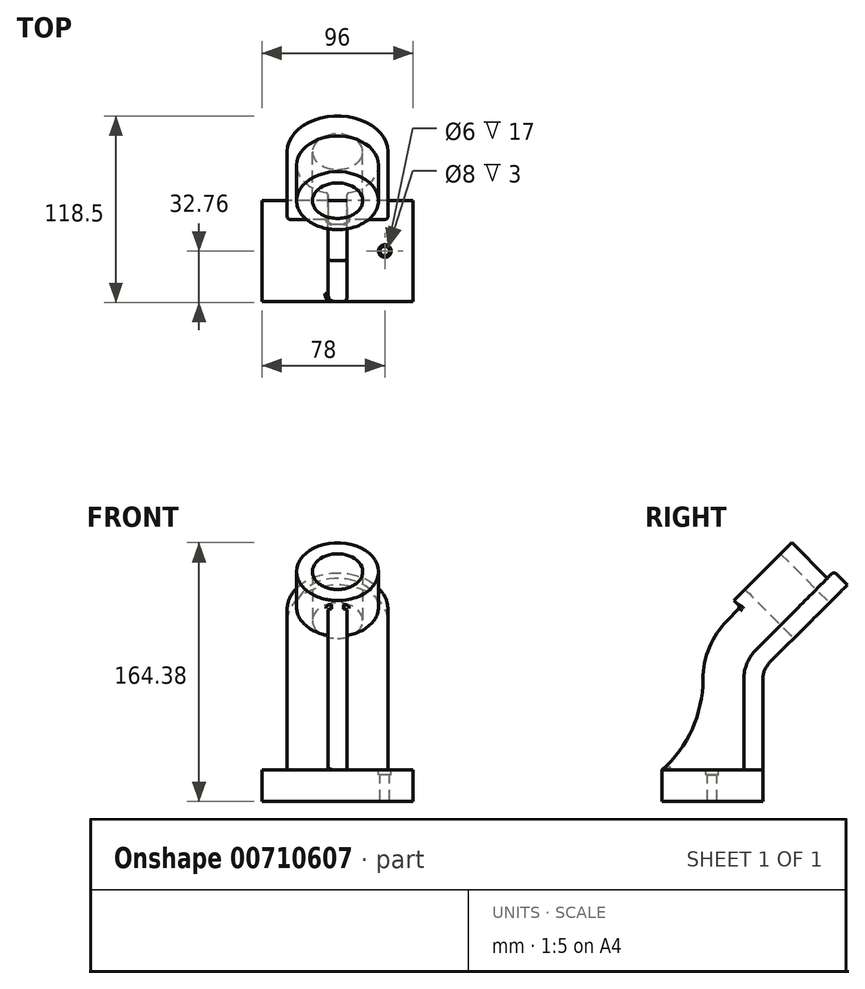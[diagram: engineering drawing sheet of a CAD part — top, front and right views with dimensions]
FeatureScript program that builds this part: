
annotation { "Feature Type Name" : "Feature", "Feature Type Description" : "" }
export const myFeature = defineFeature(function(context is Context, id is Id, definition is map)
    precondition{}
    {
        {
            var Q0;
            Q0=qCreatedBy(makeId("Top.planeOp"),FACE);
            var sketch = newSketch(context, id + "F0", { "sketchPlane" : qUnion([Q0])});
            skLineSegment(sketch, "E0.bottom", {"start": v(-48, 0) * mm, "end": v(48, 0) * mm});
            skLineSegment(sketch, "E0.top", {"start": v(-48, -64) * mm, "end": v(48, -64) * mm});
            skLineSegment(sketch, "E0.left", {"start": v(-48, 0) * mm, "end": v(-48, -64) * mm});
            skLineSegment(sketch, "E0.right", {"start": v(48, 0) * mm, "end": v(48, -64) * mm});
            skPoint(sketch, "E1", {"position": v(0, 0) * mm});
            skSolve(sketch);
        }
        {
            var Q0;
            Q0 = qSketchRegion(id + "F0", true);
            extrude(context, id + "F1", {"entities" : qUnion([Q0]), "depth" : 20 * mm, "offsetDistance" : 25 * mm});
        }
        {
            var Q0;
            Q0=qCreatedBy(makeId("Right.planeOp"),FACE);
            var sketch = newSketch(context, id + "F2", { "sketchPlane" : qUnion([Q0])});
            skLineSegment(sketch, "E2", {"start": v(0, 20) * mm, "end": v(0, 77.56) * mm});
            skLineSegment(sketch, "E3", {"start": v(4.4, 88.17) * mm, "end": v(53.74, 137.51) * mm});
            skLineSegment(sketch, "E4", {"start": v(31.11, 114.89) * mm, "end": v(0, 146) * mm, "construction": true});
            skPoint(sketch, "E5.visualSharp", {"position": v(0, 83.77) * mm});
            skArc(sketch, "E5.filletArc", {"start": v(4.4, 88.17) * mm, "mid": v(1.14, 83.3) * mm, "end": v(0, 77.56) * mm});
            skLineSegment(sketch, "E6.0", {"start": v(-4.1, 96.65) * mm, "end": v(45.25, 146) * mm});
            skArc(sketch, "E6.1", {"start": v(-4.1, 96.65) * mm, "mid": v(-9.94, 87.9) * mm, "end": v(-12, 77.56) * mm});
            skLineSegment(sketch, "E6.2", {"start": v(-12, 20) * mm, "end": v(-12, 77.56) * mm});
            skLineSegment(sketch, "E7", {"start": v(45.25, 146) * mm, "end": v(53.74, 137.51) * mm});
            skLineSegment(sketch, "E8", {"start": v(0, 20) * mm, "end": v(-12, 20) * mm});
            skPoint(sketch, "E9", {"position": v(22.63, 123.37) * mm});
            skSolve(sketch);
        }
        {
            var Q0;
            Q0 = qSketchRegion(id + "F2", true);
            extrude(context, id + "F3", {"entities" : qUnion([Q0]), "operationType" : NewBodyOperationType.ADD, "endBound" : BoundingType.SYMMETRIC, "depth" : 64 * mm, "offsetDistance" : 25 * mm});
        }
        {
            var Q0;
            Q0=makeQuery(id+"F3.opExtrude","CAP_EDGE",EDGE,{"disambiguationData":[OSD([sQuery(id+"F2.wireOp",EDGE,"E7")])],"isStart":false});
            var Q1;
            Q1=makeQuery(id+"F3.opExtrude","CAP_EDGE",EDGE,{"disambiguationData":[OSD([sQuery(id+"F2.wireOp",EDGE,"E7")])],"isStart":true});
            fillet(context, id + "F4", {"entities" : qUnion([Q0, Q1]), "radius" : 32 * mm, "tangentPropagation" : true, "allowEdgeOverflow" : false});
        }
        {
            var Q0;
            Q0=makeQuery(id+"F3.opExtrude","SWEPT_FACE",FACE,{"disambiguationData":[OSD([sQuery(id+"F2.wireOp",EDGE,"E6.0")])]});
            var sketch = newSketch(context, id + "F5", { "sketchPlane" : qUnion([Q0])});
            skCircle(sketch, "E10", {"center": v(0, 103.24) * mm, "radius": 16 * mm});
            skCircle(sketch, "E11", {"center": v(0, 103.24) * mm, "radius": 26 * mm});
            skSolve(sketch);
        }
        {
            var Q0;
            Q0 = qSketchRegion(id + "F5", true);
            var Q1;
            Q1=sQuery(id+"F2.wireOp",VERTEX,"E4.end");
            extrude(context, id + "F6", {"entities" : qUnion([Q0]), "operationType" : NewBodyOperationType.ADD, "endBound" : BoundingType.UP_TO_VERTEX, "depth" : 32 * mm, "endBoundEntityVertex" : qUnion([Q1]), "offsetDistance" : 25 * mm});
        }
        {
            var Q0;
            Q0=makeQuery(id+"F5.imprint","IMPRINT",FACE,{"disambiguationData":[TD([[makeQuery(id+"F5.imprint","IMPRINT",EDGE,{"derivedFrom":sQuery(id+"F5.wireOp",EDGE,"E10")}),1.0]])]});
            extrude(context, id + "F7", {"entities" : qUnion([Q0]), "operationType" : NewBodyOperationType.REMOVE, "endBound" : BoundingType.THROUGH_ALL, "oppositeDirection" : true, "depth" : 25 * mm, "offsetDistance" : 25 * mm});
        }
        {
            var Q0;
            Q0=qCreatedBy(makeId("Right.planeOp"),FACE);
            var sketch = newSketch(context, id + "F8", { "sketchPlane" : qUnion([Q0])});
            skLineSegment(sketch, "E12.0", {"start": v(-11.31, 134.69) * mm, "end": v(11.31, 157.31) * mm, "construction": true});
            skLineSegment(sketch, "E13.0", {"start": v(-4.1, 96.65) * mm, "end": v(11.31, 112.06) * mm});
            skArc(sketch, "E14.0", {"start": v(-4.1, 96.65) * mm, "mid": v(-9.94, 87.9) * mm, "end": v(-12, 77.56) * mm});
            skLineSegment(sketch, "E15.0", {"start": v(-12, 20) * mm, "end": v(-12, 77.56) * mm});
            skLineSegment(sketch, "E16", {"start": v(-7.07, 130.44) * mm, "end": v(11.31, 112.06) * mm});
            skPoint(sketch, "E17.orphan", {"position": v(22.63, 123.37) * mm});
            skLineSegment(sketch, "E18.0", {"start": v(-22.48, 115.04) * mm, "end": v(-7.07, 130.44) * mm});
            skArc(sketch, "E18.1", {"start": v(-22.48, 115.04) * mm, "mid": v(-33.97, 97.84) * mm, "end": v(-38, 77.56) * mm});
            skArc(sketch, "E19", {"start": v(-64, 20) * mm, "mid": v(-44.8, 45.98) * mm, "end": v(-38, 77.56) * mm});
            skLineSegment(sketch, "E20", {"start": v(-64, 20) * mm, "end": v(-12, 20) * mm});
            skLineSegment(sketch, "E21", {"start": v(-38, 77.56) * mm, "end": v(-38, 77.56) * mm});
            skSolve(sketch);
        }
        {
            var Q0;
            Q0 = qSketchRegion(id + "F8", true);
            extrude(context, id + "F9", {"entities" : qUnion([Q0]), "operationType" : NewBodyOperationType.ADD, "endBound" : BoundingType.SYMMETRIC, "depth" : 12 * mm, "offsetDistance" : 25 * mm});
        }
        {
            var Q0;
            Q0 = qSketchRegion(id + "F8", true);
            extrude(context, id + "F10", {"entities" : qUnion([Q0]), "operationType" : NewBodyOperationType.ADD, "endBound" : BoundingType.SYMMETRIC, "depth" : 12 * mm, "offsetDistance" : 25 * mm});
        }
        {
            var Q0;
            {var subQ1=sQuery(id+"F0.wireOp",EDGE,"E0.top");var subQ3=sQuery(id+"F0.wireOp",EDGE,"E0.right");var subQ4=sQuery(id+"F0.wireOp",EDGE,"E0.bottom");Q0=makeQuery(id+"F9.boolean.opBoolean","SPLIT",FACE,{"disambiguationData":[TD([makeQuery(id+"F1.opExtrude","SWEPT_FACE",FACE,{"disambiguationData":[OSD([subQ3])]})])],"derivedFrom":makeQuery(id+"F1.opExtrude","CAP_FACE",FACE,{"disambiguationData":[OSD([subQ4,subQ1,sQuery(id+"F0.wireOp",EDGE,"E0.left"),subQ3])],"isStart":false})});}
            var sketch = newSketch(context, id + "F11", { "sketchPlane" : qUnion([Q0])});
            skCircle(sketch, "E22", {"center": v(30, -32) * mm, "radius": 3 * mm});
            skCircle(sketch, "E23", {"center": v(30, -32) * mm, "radius": 4 * mm});
            skLineSegment(sketch, "E24", {"start": v(0, 0) * mm, "end": v(0, -64) * mm, "construction": true});
            skSolve(sketch);
        }
        {
            var Q0;
            Q0=makeQuery(id+"F11.imprint","IMPRINT",FACE,{"disambiguationData":[TD([[makeQuery(id+"F11.imprint","IMPRINT",EDGE,{"derivedFrom":sQuery(id+"F11.wireOp",EDGE,"E22")}),1.0]])]});
            extrude(context, id + "F12", {"entities" : qUnion([Q0]), "operationType" : NewBodyOperationType.REMOVE, "endBound" : BoundingType.THROUGH_ALL, "oppositeDirection" : true, "depth" : 25 * mm, "offsetDistance" : 25 * mm});
        }
        {
            var Q0;
            Q0=makeQuery(id+"F11.imprint","IMPRINT",FACE,{"disambiguationData":[TD([[makeQuery(id+"F11.imprint","IMPRINT",EDGE,{"derivedFrom":sQuery(id+"F11.wireOp",EDGE,"E22")}),-1.0]])]});
            extrude(context, id + "F13", {"entities" : qUnion([Q0]), "operationType" : NewBodyOperationType.REMOVE, "oppositeDirection" : true, "depth" : 3 * mm, "offsetDistance" : 25 * mm});
        }
        {
            var Q0;
            Q0=makeQuery(id+"F6.opExtrude","CAP_EDGE",EDGE,{"disambiguationData":[OSD([sQuery(id+"F5.wireOp",EDGE,"E11")])],"isStart":true});
            var Q1;
            Q1=makeQuery(id+"F9.opExtrude","CAP_EDGE",EDGE,{"disambiguationData":[OSD([sQuery(id+"F8.wireOp",EDGE,"E13.0")])],"isStart":true});
            var Q2;
            Q2=makeQuery(id+"F9.opExtrude","CAP_EDGE",EDGE,{"disambiguationData":[OSD([sQuery(id+"F8.wireOp",EDGE,"E13.0")])],"isStart":false});
            var Q3;
            Q3=makeQuery(id+"F9.boolean.opBoolean","INTERSECT",EDGE,{"derivedFrom":[makeQuery(id+"F6.opExtrude","SWEPT_FACE",FACE,{"disambiguationData":[OSD([sQuery(id+"F5.wireOp",EDGE,"E11")])]}),makeQuery(id+"F9.opExtrude","SWEPT_FACE",FACE,{"disambiguationData":[OSD([sQuery(id+"F8.wireOp",EDGE,"E18.0")])]})]});
            var Q4;
            Q4=makeQuery(id+"F9.boolean.opBoolean","INTERSECT",EDGE,{"derivedFrom":[makeQuery(id+"F6.opExtrude","SWEPT_FACE",FACE,{"disambiguationData":[OSD([sQuery(id+"F5.wireOp",EDGE,"E11")])]}),makeQuery(id+"F9.opExtrude","CAP_FACE",FACE,{"disambiguationData":[OSD([sQuery(id+"F8.wireOp",EDGE,"E13.0"),sQuery(id+"F8.wireOp",EDGE,"E14.0"),sQuery(id+"F8.wireOp",EDGE,"E15.0"),sQuery(id+"F8.wireOp",EDGE,"E16"),sQuery(id+"F8.wireOp",EDGE,"E18.0"),sQuery(id+"F8.wireOp",EDGE,"E18.1"),sQuery(id+"F8.wireOp",EDGE,"E19"),sQuery(id+"F8.wireOp",EDGE,"E20"),sQuery(id+"F8.wireOp",EDGE,"E21")])],"isStart":true})]});
            var Q5;
            Q5=makeQuery(id+"F9.boolean.opBoolean","INTERSECT",EDGE,{"derivedFrom":[makeQuery(id+"F6.opExtrude","SWEPT_FACE",FACE,{"disambiguationData":[OSD([sQuery(id+"F5.wireOp",EDGE,"E11")])]}),makeQuery(id+"F9.opExtrude","CAP_FACE",FACE,{"disambiguationData":[OSD([sQuery(id+"F8.wireOp",EDGE,"E13.0"),sQuery(id+"F8.wireOp",EDGE,"E14.0"),sQuery(id+"F8.wireOp",EDGE,"E15.0"),sQuery(id+"F8.wireOp",EDGE,"E16"),sQuery(id+"F8.wireOp",EDGE,"E18.0"),sQuery(id+"F8.wireOp",EDGE,"E18.1"),sQuery(id+"F8.wireOp",EDGE,"E19"),sQuery(id+"F8.wireOp",EDGE,"E20"),sQuery(id+"F8.wireOp",EDGE,"E21")])],"isStart":false})]});
            var Q6;
            Q6=makeQuery(id+"F9.opExtrude","CAP_EDGE",EDGE,{"disambiguationData":[OSD([sQuery(id+"F8.wireOp",EDGE,"E18.1")])],"isStart":false});
            var Q7;
            Q7=makeQuery(id+"F9.opExtrude","CAP_EDGE",EDGE,{"disambiguationData":[OSD([sQuery(id+"F8.wireOp",EDGE,"E18.1")])],"isStart":true});
            var Q8;
            Q8=makeQuery(id+"F9.opExtrude","CAP_EDGE",EDGE,{"disambiguationData":[OSD([sQuery(id+"F8.wireOp",EDGE,"E19")])],"isStart":true});
            var Q9;
            Q9=makeQuery(id+"F9.opExtrude","CAP_EDGE",EDGE,{"disambiguationData":[OSD([sQuery(id+"F8.wireOp",EDGE,"E19")])],"isStart":false});
            var Q10;
            Q10=makeQuery(id+"F3.opExtrude","CAP_EDGE",EDGE,{"disambiguationData":[OSD([sQuery(id+"F2.wireOp",EDGE,"E6.0")])],"isStart":false});
            fillet(context, id + "F14", {"entities" : qUnion([Q0, Q1, Q2, Q3, Q4, Q5, Q6, Q7, Q8, Q9, Q10]), "radius" : 2 * mm, "tangentPropagation" : true, "allowEdgeOverflow" : false});
        }
        {
            var Q0;
            Q0=makeQuery(id+"F9.opExtrude","CAP_EDGE",EDGE,{"disambiguationData":[OSD([sQuery(id+"F8.wireOp",EDGE,"E20")])],"isStart":true});
            var Q1;
            Q1=makeQuery(id+"F9.opExtrude","CAP_EDGE",EDGE,{"disambiguationData":[OSD([sQuery(id+"F8.wireOp",EDGE,"E20")])],"isStart":false});
            var Q2;
            Q2=makeQuery(id+"F3.opExtrude","CAP_EDGE",EDGE,{"disambiguationData":[OSD([sQuery(id+"F2.wireOp",EDGE,"E8")])],"isStart":true});
            fillet(context, id + "F15", {"entities" : qUnion([Q0, Q1, Q2]), "radius" : 2 * mm, "tangentPropagation" : true, "allowEdgeOverflow" : false});
        }
    });
